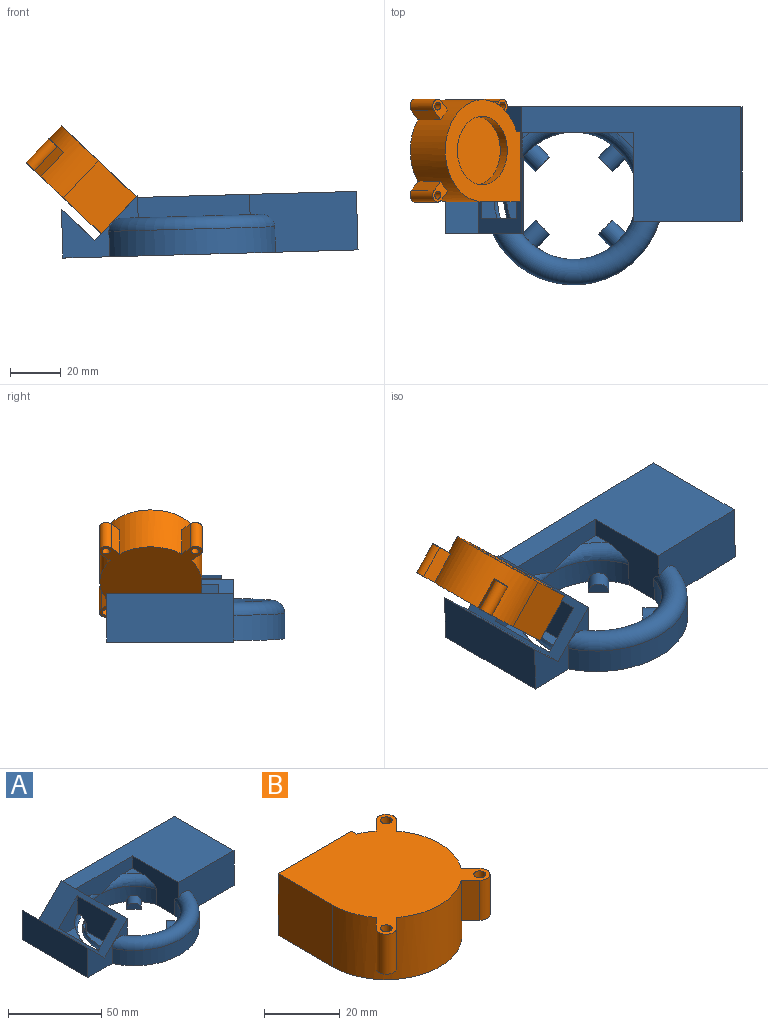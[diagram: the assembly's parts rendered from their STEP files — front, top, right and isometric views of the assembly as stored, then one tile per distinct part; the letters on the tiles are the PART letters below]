
ASSEMBLY  parts=2 mates=1
PART A: 39 faces, bbox 120x78.2x28.9 mm
  f0: plane 116x23.79mm, normal (0,1,0), area 2403.6mm2, adj f2,f3,f6,f15,f21,f28,f29
  f1: plane 31.25x25.04mm, normal (0,-1,0), area 263.8mm2, adj f2,f3,f6,f11,f14,f28,f29
  f2: plane 51.38x25.17mm, normal (1,0,0), area 816.5mm2, adj f0,f1,f4,f7,f8,f9,f10,f12
  f3: plane 50x19.24mm, normal (-1,0,0), area 961.8mm2, adj f0,f1,f6,f29
  f4: plane 55.5x55.5mm, normal (0,0,-1), area 803.7mm2, adj f2,f5,f7,f8,f9,f10,f19,f22
  f5: cylinder r=4mm len=10.73mm, axis (0.71,-0.71,0), area 90.2mm2, adj f4,f9,f25
  f6: plane 116x70mm, normal (0,0,-1), area 3663.2mm2, adj f0,f1,f3,f11,f20,f21,f27,f36
  f7: cylinder r=4mm len=10.78mm, axis (-0.71,-0.71,0), area 90.3mm2, adj f2,f4,f9,f24
  f8: cylinder r=25mm len=44mm, axis (0,0,1), area 503.7mm2, adj f2,f4,f10,f13,f18,f19,f22
  f9: cylinder r=25mm len=44mm, axis (0,0,1), area 503.8mm2, adj f2,f4,f5,f7,f14,f19
  f10: cylinder r=4mm len=10.78mm, axis (0.71,-0.71,0), area 90.3mm2, adj f2,f4,f8,f26
  f11: cylinder r=35mm len=65.16mm, axis (0,0,1), area 843.1mm2, adj f1,f6,f14,f20
  f12: plane 3.42x2.64mm, normal (0,0,1), area 4.3mm2, adj f2,f13,f16
  f13: torus R=30mm, axis (0,0,-1), area 110.1mm2, adj f2,f8,f12,f16
  f14: torus R=30mm, axis (0,0,-1), area 1075.4mm2, adj f1,f9,f11,f19,f20
  f15: plane 86x45mm, normal (0,0,1), area 2330mm2, adj f0,f2,f16,f19,f20,f21
  f16: plane 45.21x14.22mm, normal (0,-1,0), area 414.8mm2, adj f2,f12,f13,f15,f17,f18,f19
  f17: plane 7.42x7mm, normal (0,0,1), area 23mm2, adj f16,f18,f19
  f18: torus R=30mm, axis (0,0,-1), area 168.3mm2, adj f8,f16,f17,f19
  f19: plane 36.4x24.4mm, normal (-1,0,0), area 513.5mm2, adj f4,f8,f9,f14,f15,f16,f17,f18
  f20: plane 42.8x23.79mm, normal (0,-1,0), area 831.1mm2, adj f6,f11,f14,f15,f19,f21
  f21: plane 45x23mm, normal (1,0,0), area 1035mm2, adj f0,f6,f15,f20
  f22: cylinder r=4mm len=10.73mm, axis (-0.71,-0.71,0), area 90.2mm2, adj f4,f8,f23
  f23: plane 5.66x5.66mm, normal (-0.71,-0.71,0), area 25.1mm2, adj f4,f22
  f24: plane 5.66x5.66mm, normal (0.71,0.71,0), area 25.1mm2, adj f4,f7
  f25: plane 5.66x5.66mm, normal (-0.71,0.71,0), area 25.1mm2, adj f4,f5
  f26: plane 5.66x5.66mm, normal (0.71,-0.71,0), area 9.4mm2, adj f4,f10,f37,f38
  f27: bspline ~63.67x63.43mm, area 3892.5mm2, adj f4,f6,f30,f31,f33,f34,f35,f37
  f28: plane 50x17.28mm, normal (-0.71,0,0.71), area 621.9mm2, adj f0,f1,f2,f29,f32,f33,f34,f35
  f29: plane 50x12.72mm, normal (0.71,0,0.71), area 897.6mm2, adj f0,f1,f3,f28,f36
  f30: plane 25.84x6.62mm, normal (0,0,1), area 78.8mm2, adj f27,f34,f35
  f31: plane 34.01x16.73mm, normal (0,0,1), area 197.9mm2, adj f27,f32,f33,f34
  f32: plane 30x5.58mm, normal (1,0,0), area 167.3mm2, adj f28,f31,f33,f34
  f33: plane 19.72x14.14mm, normal (0,-1,0), area 166.2mm2, adj f27,f28,f31,f32,f35
  f34: plane 19.72x14.14mm, normal (0,1,0), area 133.6mm2, adj f27,f28,f30,f31,f32,f35
  f35: plane 30x19.72mm, normal (-1,0,0), area 537.5mm2, adj f27,f28,f30,f33,f34
  f36: cylinder r=0.78mm len=10.08mm, axis (0.71,0,0.71), area 58mm2, adj f6,f29
  f37: plane 11.84x11.84mm, normal (0,0,1), area 67.2mm2, adj f26,f27,f38
  f38: cylinder r=3.5mm len=11.66mm, axis (0.71,-0.71,0), area 95.5mm2, adj f26,f27,f37
PART B: 28 faces, bbox 40.4x40.7x20 mm
  f0: cylinder r=20mm len=40mm, axis (0,0,-1), area 1520mm2, adj f1,f2,f3,f5,f6,f7,f8,f9
  f1: plane 40.7x40.4mm, normal (0,0,1), area 1449.4mm2, adj f0,f3,f4,f5,f6,f7,f9,f10
  f2: plane 40.5x40mm, normal (0,0,-1), area 787.3mm2, adj f0,f3,f4,f5,f26
  f3: plane 20x1.96mm, normal (1,0,0), area 39.2mm2, adj f0,f1,f2,f4
  f4: plane 27.5x20mm, normal (0,1,0), area 125.2mm2, adj f1,f2,f3,f5,f21,f22,f23,f24
  f5: plane 20.5x20mm, normal (-1,0,0), area 410mm2, adj f0,f1,f2,f4
  f6: plane 13x3.49mm, normal (-0.71,0.71,0), area 64.1mm2, adj f0,f1,f8,f15
  f7: plane 13x3.49mm, normal (0.71,-0.71,0), area 64.1mm2, adj f0,f1,f8,f15
  f8: plane 8.1x8.1mm, normal (0,0,-1), area 29.9mm2, adj f0,f6,f7,f15,f18
  f9: plane 13x3.49mm, normal (0.71,0.71,0), area 64.1mm2, adj f0,f1,f11,f16
  f10: plane 13x3.49mm, normal (-0.71,-0.71,0), area 64.1mm2, adj f0,f1,f11,f16
  f11: plane 8.1x8.1mm, normal (0,0,-1), area 29.9mm2, adj f0,f9,f10,f16,f19
  f12: plane 13x3.49mm, normal (0.71,-0.71,0), area 64.1mm2, adj f0,f1,f14,f17
  f13: plane 13x3.49mm, normal (-0.71,0.71,0), area 64.1mm2, adj f0,f1,f14,f17
  f14: plane 8.1x8.1mm, normal (0,0,-1), area 29.9mm2, adj f0,f12,f13,f17,f20
  f15: cylinder r=2.7mm len=13mm, axis (0,0,1), area 110.3mm2, adj f1,f6,f7,f8
  f16: cylinder r=2.7mm len=13mm, axis (0,0,1), area 110.3mm2, adj f1,f9,f10,f11
  f17: cylinder r=2.7mm len=13mm, axis (0,0,1), area 110.3mm2, adj f1,f12,f13,f14
  f18: cylinder r=1.55mm len=13mm, axis (0,0,-1), area 126.6mm2, adj f1,f8
  f19: cylinder r=1.55mm len=13mm, axis (0,0,-1), area 126.6mm2, adj f1,f11
  f20: cylinder r=1.55mm len=13mm, axis (0,0,-1), area 126.6mm2, adj f1,f14
  f21: plane 24.7x5mm, normal (0,0,-1), area 123.5mm2, adj f4,f22,f24,f25
  f22: plane 17.2x5mm, normal (-1,0,0), area 86mm2, adj f4,f21,f23,f25
  f23: plane 24.7x5mm, normal (0,0,1), area 123.5mm2, adj f4,f22,f24,f25
  f24: plane 17.2x5mm, normal (1,0,0), area 86mm2, adj f4,f21,f23,f25
  f25: plane 24.7x17.2mm, normal (0,1,0), area 424.8mm2, adj f21,f22,f23,f24
  f26: cylinder r=13.5mm len=27mm, axis (0,0,-1), area 339.3mm2, adj f2,f27
  f27: plane 27x27mm, normal (0,0,-1), area 572.6mm2, adj f26
PLACE A rot(axis=(0,-1,0),1.6deg) t=(-17.92,6.25,6.93)mm
PLACE B rot(axis=(-0.68,-0.68,0.27),149.7deg) t=(-53.96,23.92,43.72)mm
MATE planar B.f4 <-> A.f28  axis (0.73,0,-0.69) through (-45.95,17.67,22.37)mm
